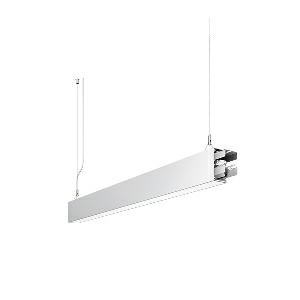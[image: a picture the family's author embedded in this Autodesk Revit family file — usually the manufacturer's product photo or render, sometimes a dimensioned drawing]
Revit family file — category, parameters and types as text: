
# Revit family: idoo_line_-_ilp_2000_830_d_sta_00805710_61ff
name_source: partatom
category: Lighting Fixtures
units: mm (PartAtom-declared; Revit-internal decimal feet)

## family parameters
Cut with Voids When Loaded = No
Host = Face
Light Source = No
Part Type = Normal
Room Calculation Point = No
Round Connector Dimension = Use Diameter
Shared = No

## types (1)
- IDOO.line - ILP 2000/830/D STA (1 x LED, 2250 lm, 3000K)
    Apparent Load = 17 VA
    Approval mark = CE
    CIE Flux Codes = 66 91 98 40 100
    Color Rendering = 80-89
    Color Temperature = 3000K
    Control Gear = Electronic ballast
    Default Elevation = 1800 mm
    Description = ILP 2000/830/D|Suspended luminaire|light source: LED|connected load: 220-240 V, 50/60 Hz|Power consumption: approx. 17 W|standby: approx. 0,20|luminous flux: 2250 lm|luminous efficacy: 132 lm/W|light distribution: Direct/indirect|direct ratio: approx. 40 %|colour temperature: Warm white, ca. 3000 K|color rendering index (CRI): >= 80|chromaticity tolerance:  3 SDCM|System of protection: IP 40|technology: Continuously dimmable|luminaire body|material: Sectional aluminium|colour: White|lamp cover: Acrylic (PMMA), Clear|mains lead: 2.00 m With free stranded wires|Fastening: Steel cable 0.3 - 0.7 m|glare control: Prism aperture|luminance(L65): <= 2700 cd/m|unified glare rating(4H 8H): <=  16|special features: DALI Load 1x, TouchDIM - dimming via standard switch, Direct and indirect light switchable together, Through-wired, up to 18 m on one mains connection, Flicker-free, Suitable as emergency lighting, Start luminaire with mains connection, Mechanical and electrical connection of the individual modules without tools|
    Frequency = 50 Hz
    Height = 110 mm
    Lamp = 1 x LED
    Lamp Light Flux = 2250 lm
    Lamp count = 1
    Length = 848 mm
    Luminous efficacy = 132 lm/W
    Manufacturer = Waldmann
    ModVariant = No
    Model = 00805710
    Mounting Place = Ceiling
    Mounting Type = Pendant
    Number of Poles = 1
    OnlyDefault = Yes
    Power Factor = 1
    Product Name = IDOO.line - ILP 2000/830/D STA
    Product group = Suspended luminaire
    ProductGroupID = 9
    Protection Class = Protection class I
    Protection Degree = IP 40
    RLX_Detail_Level = 1
    RLX_Emergency_Light_Flux = 0 lm
    RLX_Emergency_Type = 0
    RLX_Emergency_Type_DB = No
    RlxData = <blob elided: 19545 chars, md5=c8afff43>
    Socket = socket
    Standby Power = 0 W
    System Light Flux = 2250 lm
    System Power = 17 W
    Type Comments = Product without accessories
    Type Image = 113295000-00692543.jpg
    URL = http://relux.com
    VarID = ---
    Voltage = 230 V
    Voltage Range = 220-240 V
    Weight = 0.00 kg
    Width = 60 mm  [stored 0.19685 ft]

note: [stored X ft] marks values corroborated as IEEE doubles in the binary element streams (Revit-internal decimal feet)

## geometry (parser evidence)
native form markers: Blend x4, Sweep x15
no freeform markers — native parametric forms only
